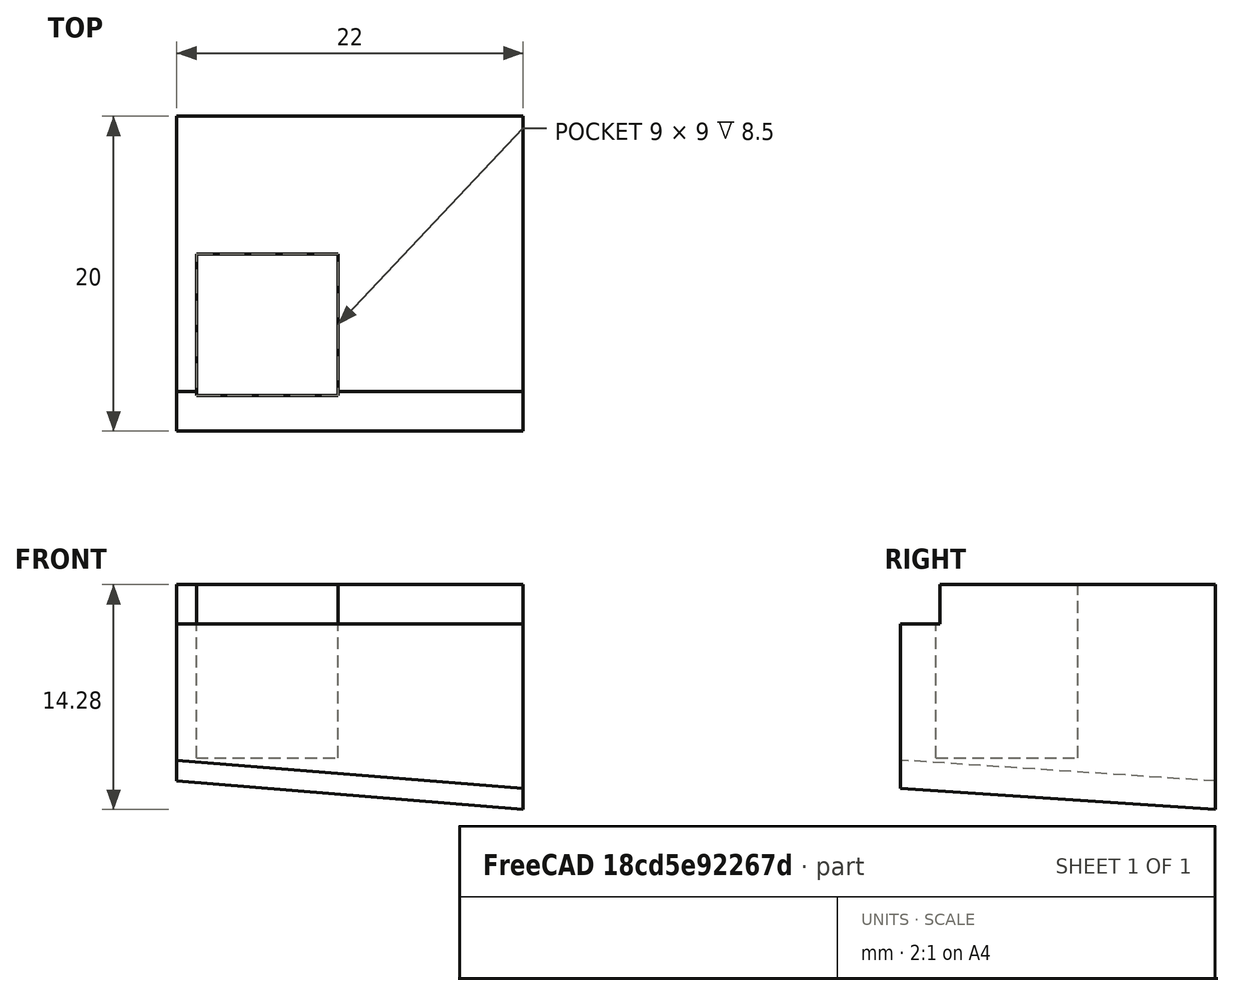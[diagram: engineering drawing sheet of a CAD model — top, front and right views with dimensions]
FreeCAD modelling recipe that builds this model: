
FCSTD DOCUMENT  (FreeCAD 0.16R6707 (Git))
Label: US_bracket_left
License: All rights reserved
LicenseURL: http://en.wikipedia.org/wiki/All_rights_reserved
objects: Part::Box×4, Part::Cut×3
note: 7 computed .brp shape members not serialized (recipe doc carries the construction recipe); baked Part::Feature solids carry a one-line shape summary decoded from their .brp

FEATURE [Part::Box] Box  label="Cube"
  Height = 15
  Length = 22
  Width = 20
FEATURE [Part::Box] Box001  label="Cube001"
  Height = 11
  Length = 9
  Placement = pos=(1.25,2.25,4) rot=(0,0,1;0rad)
  Width = 9
FEATURE [Part::Cut] Cut
  Base = -> Box
  Tool = -> Box001
FEATURE [Part::Box] Box002  label="Cube002"
  Height = 2.5
  Length = 22
  Placement = pos=(0,0,12.5) rot=(0,0,1;0rad)
  Width = 2.5
FEATURE [Part::Cut] Cut001
  Base = -> Cut
  Tool = -> Box002
FEATURE [Part::Box] Box003  label="Cube003"
  Height = 10
  Length = 24
  Placement = pos=(-1,-2,-6) rot=(-0.631938,0.775019,0;0.10472rad)
  Width = 23
FEATURE [Part::Cut] Cut002
  Base = -> Cut001
  Tool = -> Box003
